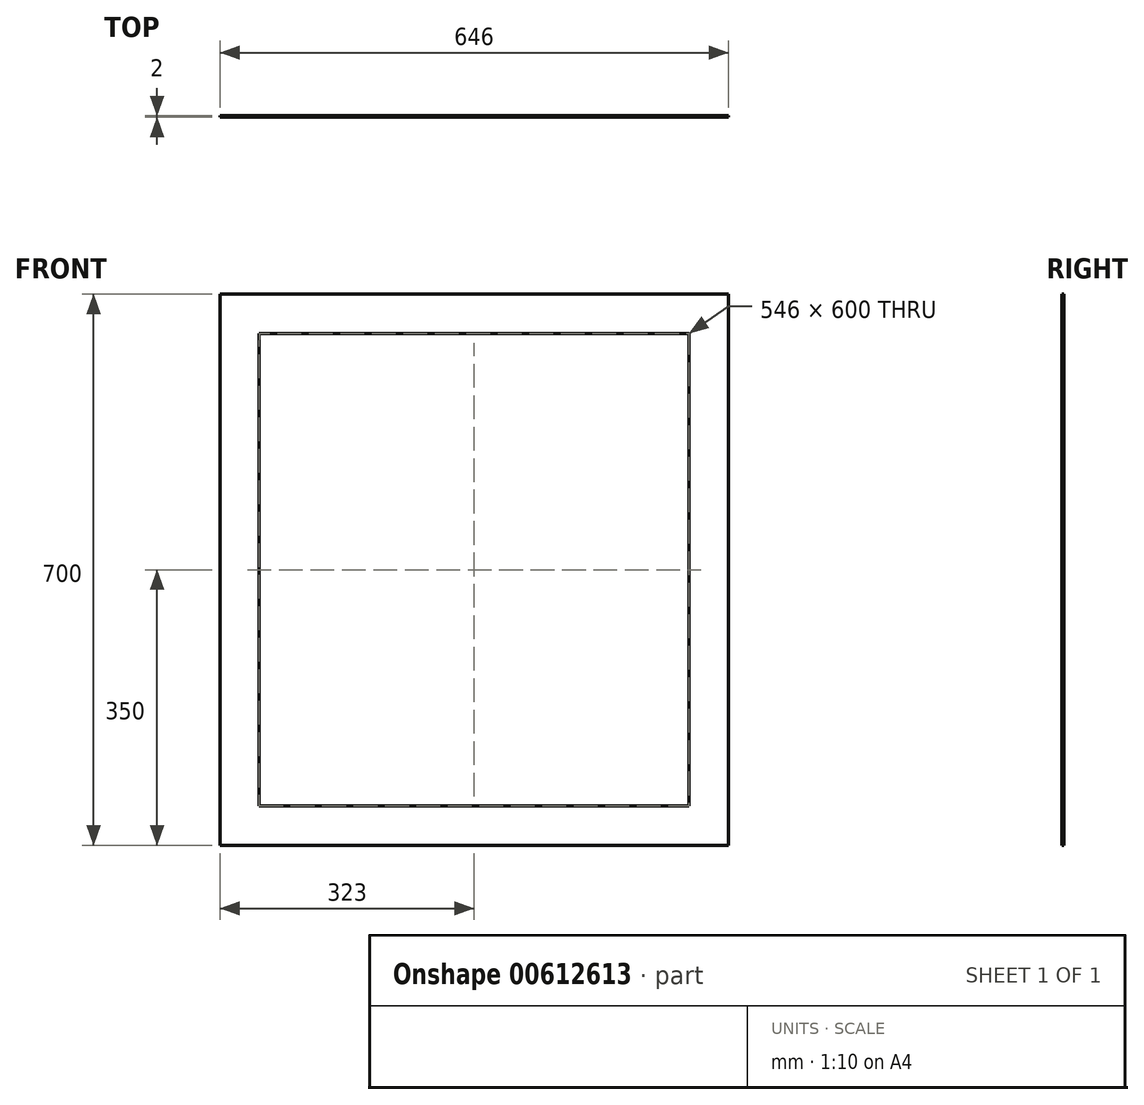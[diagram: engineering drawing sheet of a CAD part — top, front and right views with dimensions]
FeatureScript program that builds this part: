
annotation { "Feature Type Name" : "Feature", "Feature Type Description" : "" }
export const myFeature = defineFeature(function(context is Context, id is Id, definition is map)
    precondition{}
    {
        {
            var Q0;
            Q0=qCreatedBy(makeId("Front.planeOp"),FACE);
            var sketch = newSketch(context, id + "F0", { "sketchPlane" : qUnion([Q0])});
            skLineSegment(sketch, "E0.bottom", {"start": v(-323, 350) * mm, "end": v(323, 350) * mm});
            skLineSegment(sketch, "E0.top", {"start": v(-323, -350) * mm, "end": v(323, -350) * mm});
            skLineSegment(sketch, "E0.left", {"start": v(-323, 350) * mm, "end": v(-323, -350) * mm});
            skLineSegment(sketch, "E0.right", {"start": v(323, 350) * mm, "end": v(323, -350) * mm});
            skPoint(sketch, "E0.middle", {"position": v(0, 0) * mm});
            skLineSegment(sketch, "E1.bottom", {"start": v(-273, 300) * mm, "end": v(273, 300) * mm});
            skLineSegment(sketch, "E1.top", {"start": v(-273, -300) * mm, "end": v(273, -300) * mm});
            skLineSegment(sketch, "E1.left", {"start": v(-273, 300) * mm, "end": v(-273, -300) * mm});
            skLineSegment(sketch, "E1.right", {"start": v(273, 300) * mm, "end": v(273, -300) * mm});
            skSolve(sketch);
        }
        {
            var Q0;
            Q0=makeQuery(id+"F0.imprint","IMPRINT",FACE,{"disambiguationData":[TD([[makeQuery(id+"F0.imprint","IMPRINT",EDGE,{"derivedFrom":sQuery(id+"F0.wireOp",EDGE,"E0.bottom")}),-1.0]])]});
            extrude(context, id + "F1", {"entities" : qUnion([Q0]), "depth" : 2 * mm, "offsetDistance" : 25.4 * mm});
        }
    });
